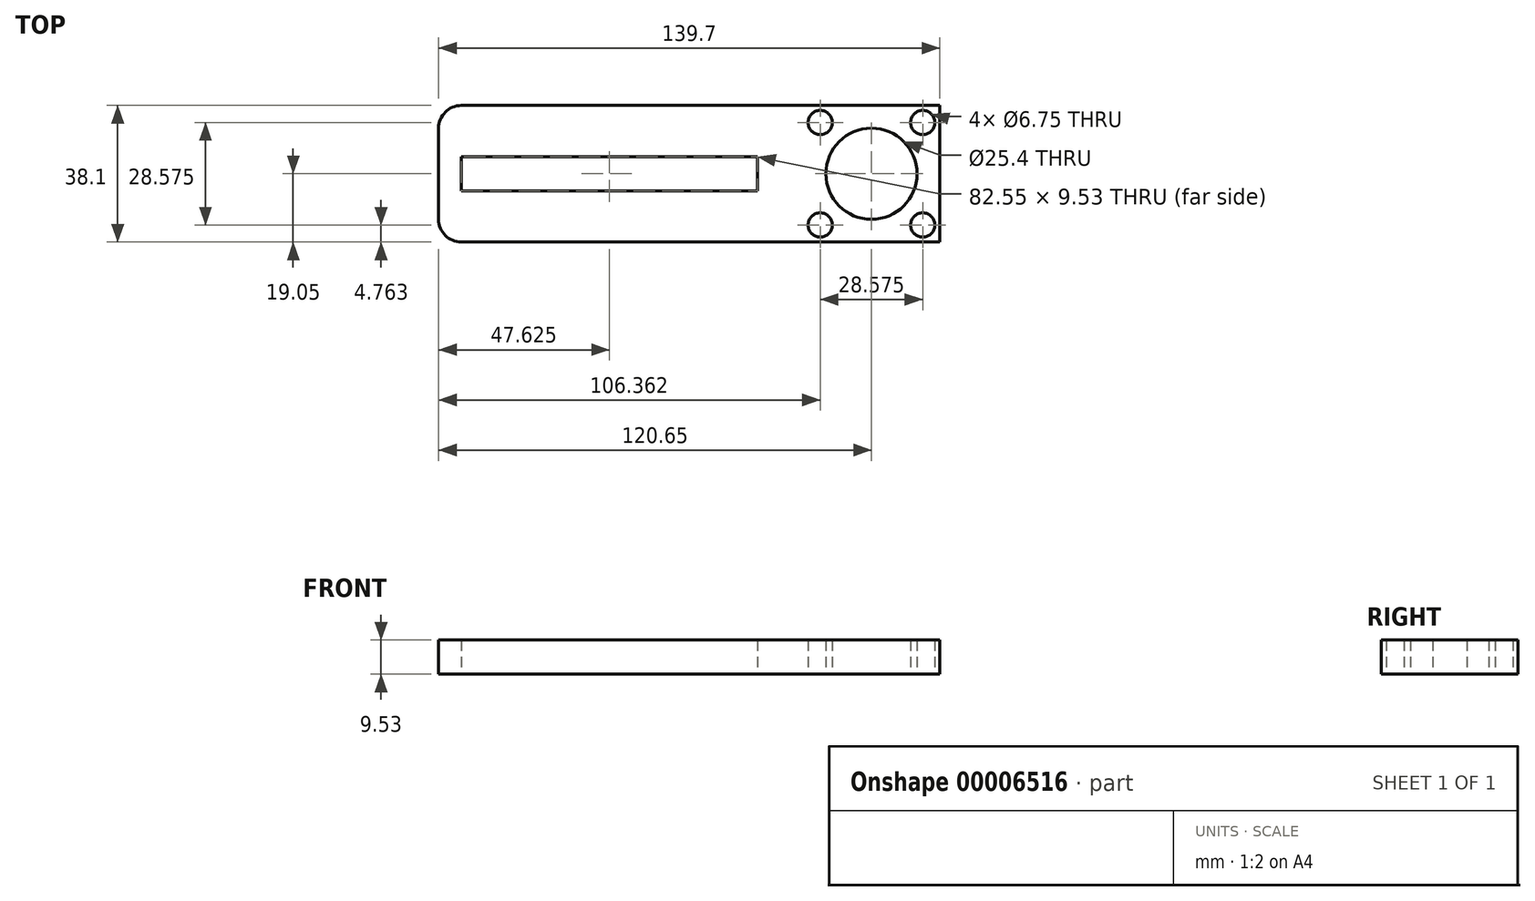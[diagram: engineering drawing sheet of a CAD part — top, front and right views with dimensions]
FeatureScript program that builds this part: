
annotation { "Feature Type Name" : "Feature", "Feature Type Description" : "" }
export const myFeature = defineFeature(function(context is Context, id is Id, definition is map)
    precondition{}
    {
        {
            var Q0;
            Q0=qCreatedBy(makeId("Top.planeOp"),FACE);
            var sketch = newSketch(context, id + "F0", { "sketchPlane" : qUnion([Q0])});
            skLineSegment(sketch, "E0.bottom", {"start": v(6.35, 0) * mm, "end": v(139.7, 0) * mm});
            skLineSegment(sketch, "E0.top", {"start": v(6.35, -38.1) * mm, "end": v(139.7, -38.1) * mm});
            skLineSegment(sketch, "E0.left", {"start": v(0, -6.35) * mm, "end": v(0, -31.75) * mm});
            skLineSegment(sketch, "E0.right", {"start": v(139.7, 0) * mm, "end": v(139.7, -38.1) * mm});
            skLineSegment(sketch, "E1.bottom", {"start": v(6.35, -14.29) * mm, "end": v(88.9, -14.29) * mm});
            skLineSegment(sketch, "E1.top", {"start": v(6.35, -23.81) * mm, "end": v(88.9, -23.81) * mm});
            skLineSegment(sketch, "E1.left", {"start": v(6.35, -14.29) * mm, "end": v(6.35, -23.81) * mm});
            skLineSegment(sketch, "E1.right", {"start": v(88.9, -14.29) * mm, "end": v(88.9, -23.81) * mm});
            skPoint(sketch, "E2", {"position": v(6.35, -19.05) * mm});
            skPoint(sketch, "E3", {"position": v(0, -19.05) * mm});
            skPoint(sketch, "E4.visualSharp", {"position": v(0, 0) * mm});
            skArc(sketch, "E4.filletArc", {"start": v(6.35, 0) * mm, "mid": v(1.86, -1.86) * mm, "end": v(0, -6.35) * mm});
            skPoint(sketch, "E5.visualSharp", {"position": v(0, -38.1) * mm});
            skArc(sketch, "E5.filletArc", {"start": v(0, -31.75) * mm, "mid": v(1.86, -36.24) * mm, "end": v(6.35, -38.1) * mm});
            skPoint(sketch, "E6", {"position": v(120.65, -19.05) * mm});
            skCircle(sketch, "E7", {"center": v(120.65, -19.05) * mm, "radius": 12.7 * mm});
            skPoint(sketch, "E8", {"position": v(134.94, -33.34) * mm});
            skCircle(sketch, "E9", {"center": v(134.94, -33.34) * mm, "radius": 3.37 * mm});
            skLineSegment(sketch, "E10", {"start": v(0, -19.05) * mm, "end": v(139.7, -19.05) * mm, "construction": true});
            skCircle(sketch, "E11.0.MirrorC", {"center": v(134.94, -4.76) * mm, "radius": 3.37 * mm});
            skLineSegment(sketch, "E12", {"start": v(120.65, 0) * mm, "end": v(120.65, -38.1) * mm, "construction": true});
            skCircle(sketch, "E13.0.MirrorC", {"center": v(106.36, -33.34) * mm, "radius": 3.37 * mm});
            skCircle(sketch, "E14.0.MirrorC", {"center": v(106.36, -4.76) * mm, "radius": 3.37 * mm});
            skSolve(sketch);
        }
        {
            var Q0;
            Q0=makeQuery(id+"F0.imprint","IMPRINT",FACE,{"disambiguationData":[TD([[makeQuery(id+"F0.imprint","IMPRINT",EDGE,{"derivedFrom":sQuery(id+"F0.wireOp",EDGE,"E0.bottom")}),-1.0]])]});
            extrude(context, id + "F1", {"entities" : qUnion([Q0]), "depth" : 9.52 * mm});
        }
    });
